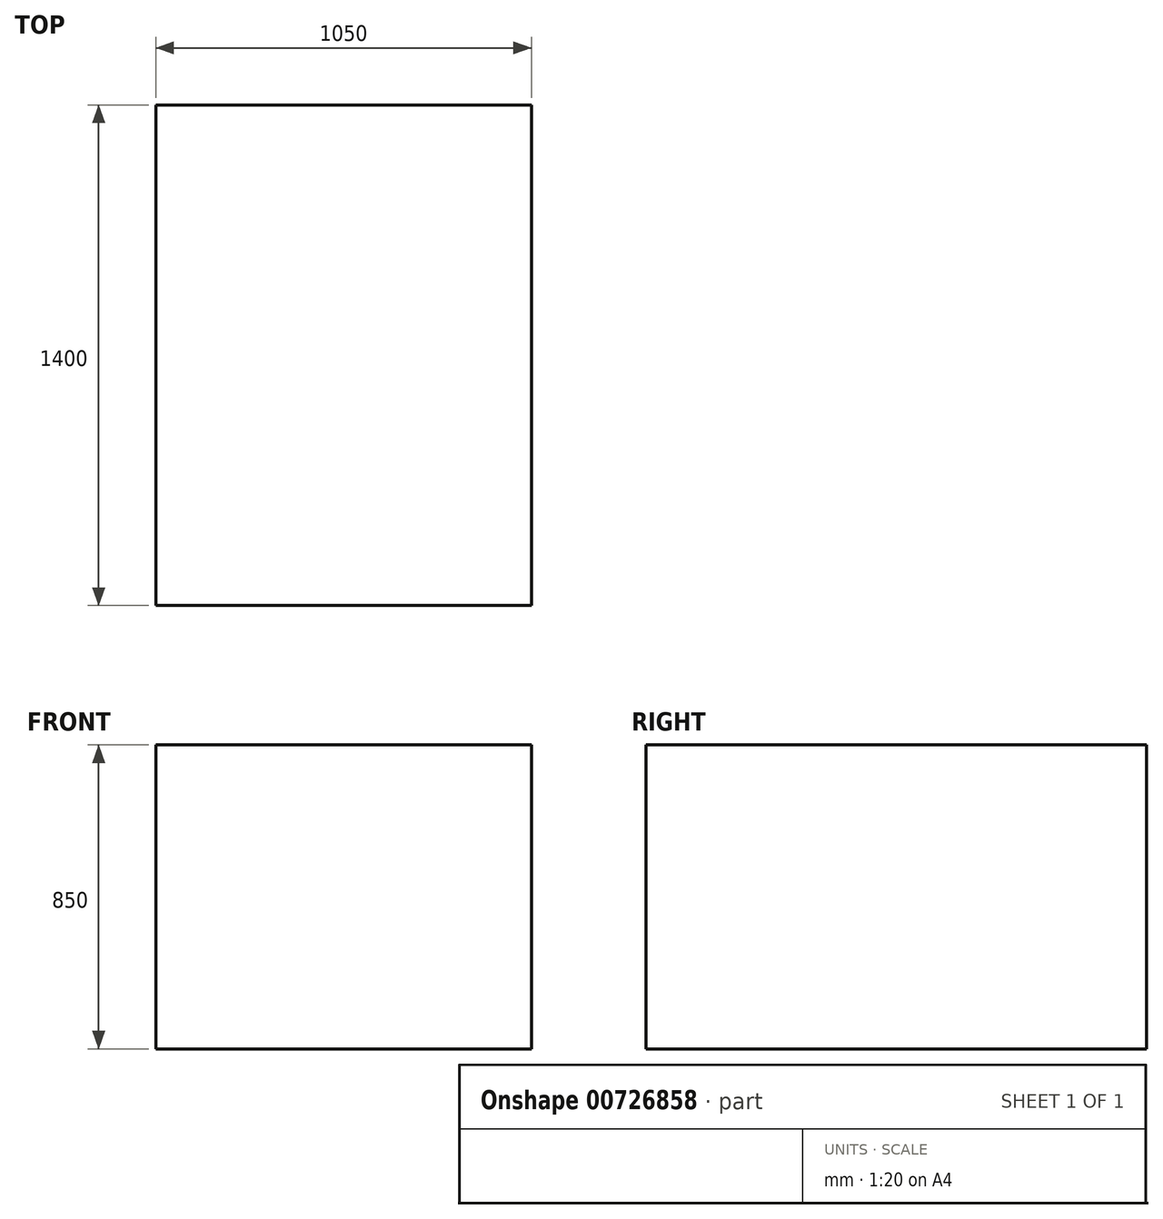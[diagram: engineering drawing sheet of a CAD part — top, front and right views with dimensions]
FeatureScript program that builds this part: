
annotation { "Feature Type Name" : "Feature", "Feature Type Description" : "" }
export const myFeature = defineFeature(function(context is Context, id is Id, definition is map)
    precondition{}
    {
        {
            var Q0;
            Q0=qCreatedBy(makeId("Front.planeOp"),FACE);
            var sketch = newSketch(context, id + "F0", { "sketchPlane" : qUnion([Q0])});
            skLineSegment(sketch, "E0.bottom", {"start": v(-538.5, 639.12) * mm, "end": v(511.5, 639.12) * mm});
            skLineSegment(sketch, "E0.top", {"start": v(-538.5, -210.88) * mm, "end": v(511.5, -210.88) * mm});
            skLineSegment(sketch, "E0.left", {"start": v(-538.5, 639.12) * mm, "end": v(-538.5, -210.88) * mm});
            skLineSegment(sketch, "E0.right", {"start": v(511.5, 639.12) * mm, "end": v(511.5, -210.88) * mm});
            skSolve(sketch);
        }
        {
            var Q0;
            Q0=makeQuery(id+"F0.imprint","IMPRINT",FACE,{"disambiguationData":[TD([[makeQuery(id+"F0.imprint","IMPRINT",EDGE,{"derivedFrom":sQuery(id+"F0.wireOp",EDGE,"E0.bottom")}),-1.0]])]});
            extrude(context, id + "F1", {"entities" : qUnion([Q0]), "oppositeDirection" : true, "depth" : 1400 * mm, "offsetDistance" : 25 * mm});
        }
    });
